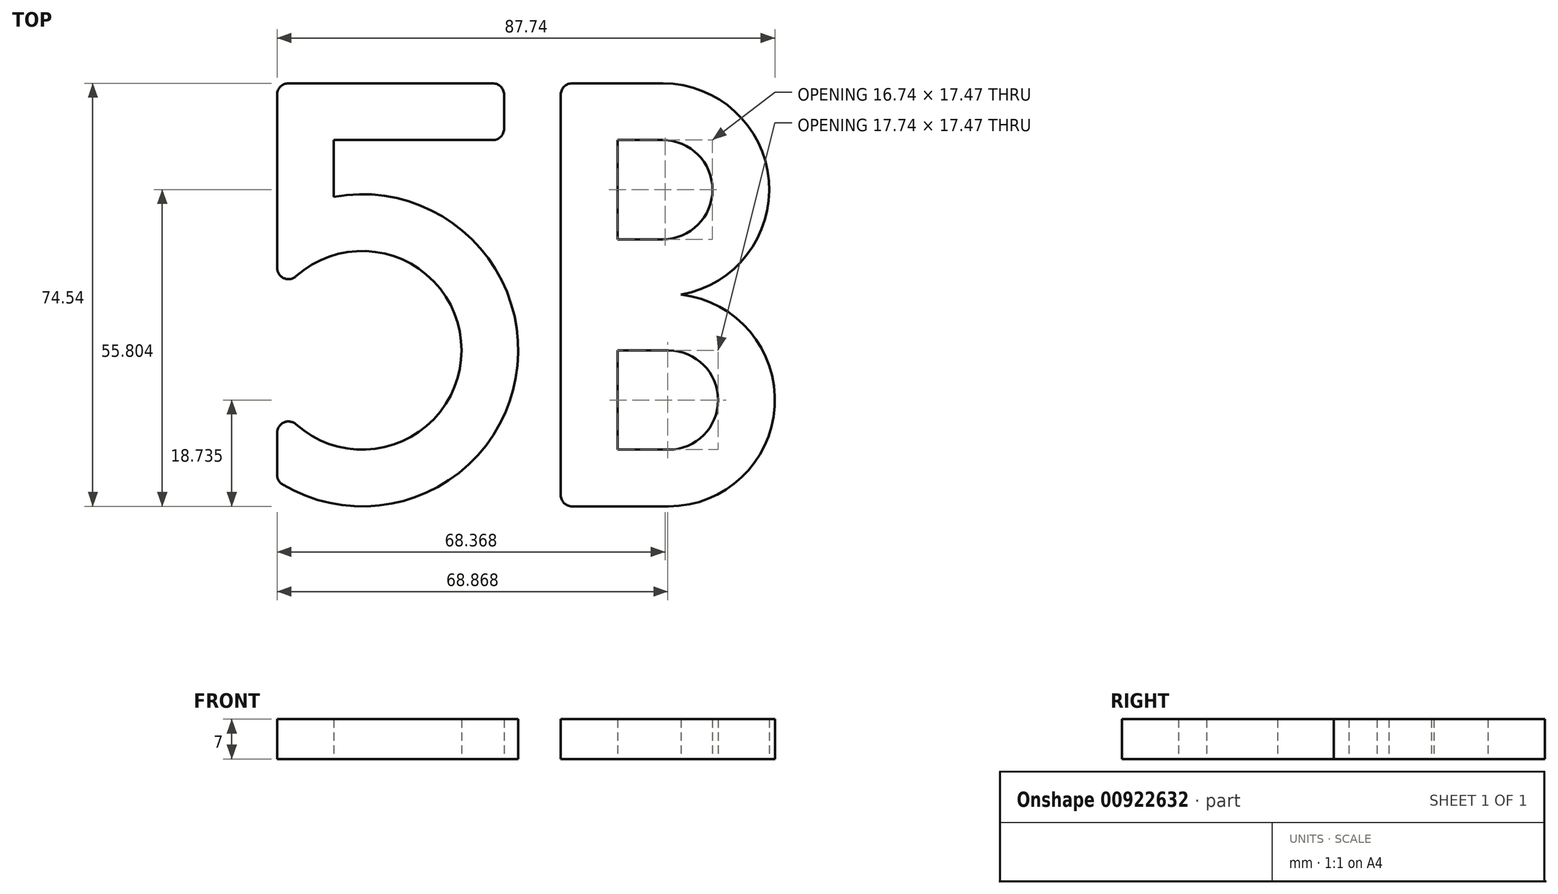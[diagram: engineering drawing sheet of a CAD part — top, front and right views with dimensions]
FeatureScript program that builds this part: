
annotation { "Feature Type Name" : "Feature", "Feature Type Description" : "" }
export const myFeature = defineFeature(function(context is Context, id is Id, definition is map)
    precondition{}
    {
        {
            var Q0;
            Q0=qCreatedBy(makeId("Top.planeOp"),FACE);
            var sketch = newSketch(context, id + "F0", { "sketchPlane" : qUnion([Q0])});
            skLineSegment(sketch, "E0", {"start": v(0, 0) * mm, "end": v(40, 0) * mm});
            skLineSegment(sketch, "E1", {"start": v(40, 0) * mm, "end": v(40, -10) * mm});
            skLineSegment(sketch, "E2", {"start": v(40, -10) * mm, "end": v(10, -10) * mm});
            skLineSegment(sketch, "E3", {"start": v(10, -10) * mm, "end": v(10, -20) * mm});
            skLineSegment(sketch, "E4", {"start": v(0, 0) * mm, "end": v(0, -38.03) * mm});
            skArc(sketch, "E5", {"start": v(0, -56.06) * mm, "mid": v(32.5, -47.04) * mm, "end": v(0, -38.03) * mm});
            skArc(sketch, "E6", {"start": v(0, -70.1) * mm, "mid": v(41.97, -52.43) * mm, "end": v(10, -20) * mm});
            skLineSegment(sketch, "E7", {"start": v(15, -47.04) * mm, "end": v(40, -47.04) * mm, "construction": true});
            skLineSegment(sketch, "E8", {"start": v(40, -10) * mm, "end": v(40, -70.86) * mm, "construction": true});
            skLineSegment(sketch, "E9", {"start": v(0, -56.06) * mm, "end": v(0, -70.1) * mm});
            skLineSegment(sketch, "E10", {"start": v(0, 0) * mm, "end": v(200.88, 0) * mm, "construction": true});
            skLineSegment(sketch, "E11", {"start": v(15.18, -74.54) * mm, "end": v(212.33, -74.54) * mm, "construction": true});
            skLineSegment(sketch, "E12", {"start": v(50, 0) * mm, "end": v(50, -74.54) * mm});
            skLineSegment(sketch, "E13", {"start": v(50, -74.54) * mm, "end": v(69, -74.54) * mm});
            skLineSegment(sketch, "E14", {"start": v(50, 0) * mm, "end": v(68, 0) * mm});
            skArc(sketch, "E15", {"start": v(68, 0) * mm, "mid": v(86.67, -17.14) * mm, "end": v(71.19, -37.2) * mm});
            skArc(sketch, "E16", {"start": v(69, -74.54) * mm, "mid": v(87.7, -56.9) * mm, "end": v(71.19, -37.2) * mm});
            skLineSegment(sketch, "E17", {"start": v(60, -10) * mm, "end": v(60, -27.47) * mm});
            skLineSegment(sketch, "E18", {"start": v(60, -47.07) * mm, "end": v(60, -64.54) * mm});
            skArc(sketch, "E19", {"start": v(68, -27.47) * mm, "mid": v(76.74, -18.74) * mm, "end": v(68, -10) * mm});
            skArc(sketch, "E20", {"start": v(69, -64.54) * mm, "mid": v(77.74, -55.8) * mm, "end": v(69, -47.07) * mm});
            skLineSegment(sketch, "E21", {"start": v(60, -10) * mm, "end": v(68, -10) * mm});
            skLineSegment(sketch, "E22", {"start": v(60, -27.47) * mm, "end": v(68, -27.47) * mm});
            skLineSegment(sketch, "E23", {"start": v(60, -47.07) * mm, "end": v(69, -47.07) * mm});
            skLineSegment(sketch, "E24", {"start": v(60, -64.54) * mm, "end": v(69, -64.54) * mm});
            skSolve(sketch);
        }
        {
            var Q0;
            Q0 = qSketchRegion(id + "F0", true);
            extrude(context, id + "F1", {"entities" : qUnion([Q0]), "depth" : 7 * mm, "offsetDistance" : 25 * mm});
        }
        {
            var Q0;
            Q0=makeQuery(id+"F1.opExtrude","SWEPT_EDGE",EDGE,{"disambiguationData":[OSD([sQuery(id+"F0.wireOp",EDGE,"E6"),sQuery(id+"F0.wireOp",EDGE,"E9")])]});
            var Q1;
            Q1=makeQuery(id+"F1.opExtrude","SWEPT_EDGE",EDGE,{"disambiguationData":[OSD([sQuery(id+"F0.wireOp",EDGE,"E5"),sQuery(id+"F0.wireOp",EDGE,"E9")])]});
            var Q2;
            Q2=makeQuery(id+"F1.opExtrude","SWEPT_EDGE",EDGE,{"disambiguationData":[OSD([sQuery(id+"F0.wireOp",EDGE,"E4"),sQuery(id+"F0.wireOp",EDGE,"E5")])]});
            var Q3;
            Q3=makeQuery(id+"F1.opExtrude","SWEPT_EDGE",EDGE,{"disambiguationData":[OSD([sQuery(id+"F0.wireOp",EDGE,"E0"),sQuery(id+"F0.wireOp",EDGE,"E4")])]});
            var Q4;
            Q4=makeQuery(id+"F1.opExtrude","SWEPT_EDGE",EDGE,{"disambiguationData":[OSD([sQuery(id+"F0.wireOp",EDGE,"E0"),sQuery(id+"F0.wireOp",EDGE,"E1")])]});
            var Q5;
            Q5=makeQuery(id+"F1.opExtrude","SWEPT_EDGE",EDGE,{"disambiguationData":[OSD([sQuery(id+"F0.wireOp",EDGE,"E1"),sQuery(id+"F0.wireOp",EDGE,"E2")])]});
            var Q6;
            Q6=makeQuery(id+"F1.opExtrude","SWEPT_EDGE",EDGE,{"disambiguationData":[OSD([sQuery(id+"F0.wireOp",EDGE,"E12"),sQuery(id+"F0.wireOp",EDGE,"E13")])]});
            var Q7;
            Q7=makeQuery(id+"F1.opExtrude","SWEPT_EDGE",EDGE,{"disambiguationData":[OSD([sQuery(id+"F0.wireOp",EDGE,"E12"),sQuery(id+"F0.wireOp",EDGE,"E14")])]});
            fillet(context, id + "F2", {"entities" : qUnion([Q0, Q1, Q2, Q3, Q4, Q5, Q6, Q7]), "radius" : 2 * mm, "tangentPropagation" : true, "allowEdgeOverflow" : false});
        }
    });
